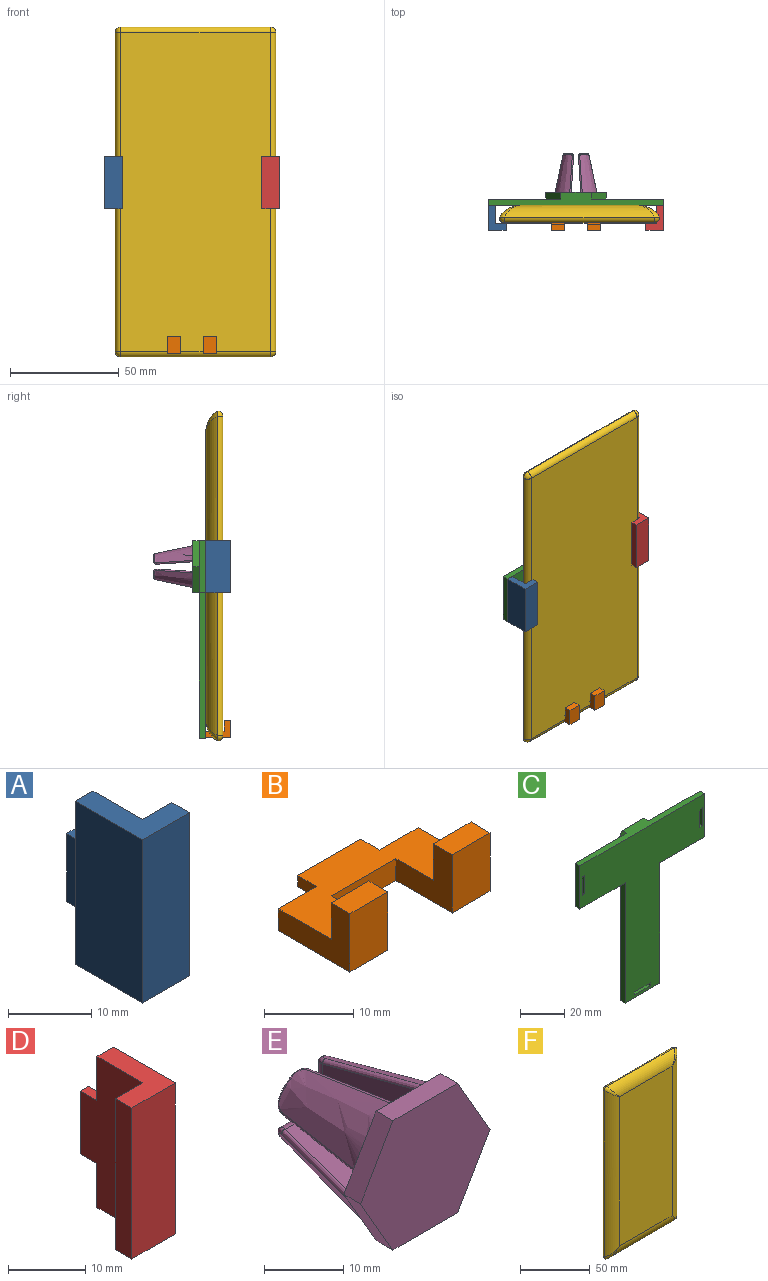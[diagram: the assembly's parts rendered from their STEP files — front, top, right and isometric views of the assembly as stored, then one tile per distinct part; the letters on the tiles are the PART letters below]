
ASSEMBLY  parts=6 mates=5
PART A: 12 faces, bbox 8x14.4x24 mm
  f0: plane 11.4x8mm, normal (0,0,-1), area 49.2mm2, adj f1,f4,f5,f6,f7,f11
  f1: plane 24x11.4mm, normal (1,0,0), area 231.6mm2, adj f0,f2,f3,f7,f8,f10,f11
  f2: plane 11.4x8mm, normal (0,0,1), area 49.2mm2, adj f1,f4,f5,f6,f7,f11
  f3: plane 10x1.5mm, normal (0,1,0), area 15mm2, adj f1,f8,f9,f10
  f4: plane 24x11.4mm, normal (-1,0,0), area 273.6mm2, adj f0,f2,f6,f11
  f5: plane 24x3mm, normal (1,0,0), area 72mm2, adj f0,f2,f6,f7
  f6: plane 24x8mm, normal (0,-1,0), area 192mm2, adj f0,f2,f4,f5
  f7: plane 24x5mm, normal (0,1,0), area 120mm2, adj f0,f1,f2,f5
  f8: plane 3x1.5mm, normal (0,0,1), area 4.5mm2, adj f1,f3,f9,f11
  f9: plane 10x3mm, normal (-1,0,0), area 30mm2, adj f3,f8,f10,f11
  f10: plane 3x1.5mm, normal (0,0,-1), area 4.5mm2, adj f1,f3,f9,f11
  f11: plane 24x3mm, normal (0,1,0), area 57mm2, adj f0,f1,f2,f4,f8,f9,f10
PART B: 18 faces, bbox 22.2x14.4x8 mm
  f0: plane 10x1.5mm, normal (0,1,0), area 15mm2, adj f1,f2,f3,f4
  f1: plane 22.2x11.4mm, normal (0,0,1), area 156.3mm2, adj f0,f3,f4,f5,f6,f7,f9,f12
  f2: plane 10x3mm, normal (0,0,-1), area 30mm2, adj f0,f3,f4,f5
  f3: plane 3x1.5mm, normal (-1,0,0), area 4.5mm2, adj f0,f1,f2,f5
  f4: plane 3x1.5mm, normal (1,0,0), area 4.5mm2, adj f0,f1,f2,f5
  f5: plane 22.2x3mm, normal (0,1,0), area 51.6mm2, adj f1,f2,f3,f4,f7,f8,f16
  f6: plane 8.9x8mm, normal (1,0,0), area 41.7mm2, adj f1,f8,f9,f10,f11,f17
  f7: plane 11.4x8mm, normal (-1,0,0), area 49.2mm2, adj f1,f5,f8,f9,f10,f11
  f8: plane 22.2x11.4mm, normal (0,0,-1), area 162.3mm2, adj f5,f6,f7,f11,f12,f15,f16,f17
  f9: plane 6x5mm, normal (0,1,0), area 30mm2, adj f1,f6,f7,f10
  f10: plane 6x3mm, normal (0,0,1), area 18mm2, adj f6,f7,f9,f11
  f11: plane 8x6mm, normal (0,-1,0), area 48mm2, adj f6,f7,f8,f10
  f12: plane 8.9x8mm, normal (-1,0,0), area 41.7mm2, adj f1,f8,f13,f14,f15,f17
  f13: plane 6x5mm, normal (0,1,0), area 30mm2, adj f1,f12,f14,f16
  f14: plane 6x3mm, normal (0,0,1), area 18mm2, adj f12,f13,f15,f16
  f15: plane 8x6mm, normal (0,-1,0), area 48mm2, adj f8,f12,f14,f16
  f16: plane 11.4x8mm, normal (1,0,0), area 49.2mm2, adj f1,f5,f8,f13,f14,f15
  f17: plane 10.2x3mm, normal (0,-1,0), area 30.6mm2, adj f1,f6,f8,f12
PART C: 35 faces, bbox 80.2x6x90.8 mm
  f0: plane 66.75x3mm, normal (-1,0,0), area 200.2mm2, adj f2,f3,f4,f5
  f1: plane 66.75x3mm, normal (1,0,0), area 200.2mm2, adj f2,f3,f4,f9
  f2: plane 22.2x3mm, normal (0,0,-1), area 66.6mm2, adj f0,f1,f3,f4
  f3: plane 90.75x80.2mm, normal (0,1,0), area 2859.3mm2, adj f0,f1,f2,f5,f6,f7,f8,f9
  f4: plane 90.75x80.2mm, normal (0,-1,0), area 3358.2mm2, adj f0,f1,f2,f5,f6,f7,f8,f9
  f5: plane 29x3mm, normal (0,0,-1), area 87mm2, adj f0,f3,f4,f8
  f6: plane 24x3mm, normal (1,0,0), area 72mm2, adj f3,f4,f7,f9
  f7: plane 80.2x6mm, normal (0,0,1), area 282.2mm2, adj f3,f4,f6,f8,f16,f17,f21
  f8: plane 24x3mm, normal (-1,0,0), area 72mm2, adj f3,f4,f5,f7
  f9: plane 29x3mm, normal (0,0,-1), area 87mm2, adj f1,f3,f4,f6
  f10: plane 10.1x5.83mm, normal (0.87,0,-0.5), area 35mm2, adj f11,f20,f21,f22
  f11: plane 10.1x5.83mm, normal (0.87,0,0.5), area 35mm2, adj f10,f12,f21,f22
  f12: plane 11.66x3mm, normal (0,0,1), area 35mm2, adj f11,f13,f21,f22
  f13: plane 10.1x5.83mm, normal (-0.87,0,0.5), area 35mm2, adj f12,f14,f21,f22
  f14: plane 10.1x5.83mm, normal (-0.87,0,-0.5), area 35mm2, adj f13,f20,f21,f22
  f15: plane 12x6.93mm, normal (-0.87,0,-0.5), area 41.6mm2, adj f3,f16,f19,f21
  f16: plane 12x6.93mm, normal (-0.87,0,0.5), area 41.6mm2, adj f3,f7,f15,f21
  f17: plane 12x6.93mm, normal (0.87,0,0.5), area 41.6mm2, adj f3,f7,f18,f21
  f18: plane 12x6.93mm, normal (0.87,0,-0.5), area 41.6mm2, adj f3,f17,f19,f21
  f19: plane 13.86x3mm, normal (0,0,-1), area 41.6mm2, adj f3,f15,f18,f21
  f20: plane 11.66x3mm, normal (0,0,-1), area 35mm2, adj f10,f14,f21,f22
  f21: plane 27.71x24mm, normal (0,1,0), area 145.5mm2, adj f7,f10,f11,f12,f13,f14,f15,f16
  f22: plane 23.33x20.2mm, normal (0,1,0), area 353.4mm2, adj f10,f11,f12,f13,f14,f20
  f23: plane 10.1x3mm, normal (1,0,0), area 30.3mm2, adj f3,f4,f24,f25
  f24: plane 3x1.6mm, normal (0,0,-1), area 4.8mm2, adj f3,f4,f23,f26
  f25: plane 3x1.6mm, normal (0,0,1), area 4.8mm2, adj f3,f4,f23,f26
  f26: plane 10.1x3mm, normal (-1,0,0), area 30.3mm2, adj f3,f4,f24,f25
  f27: plane 10.1x3mm, normal (0,0,1), area 30.3mm2, adj f3,f4,f28,f29
  f28: plane 3x1.6mm, normal (1,0,0), area 4.8mm2, adj f3,f4,f27,f30
  f29: plane 3x1.6mm, normal (-1,0,0), area 4.8mm2, adj f3,f4,f27,f30
  f30: plane 10.1x3mm, normal (0,0,-1), area 30.3mm2, adj f3,f4,f28,f29
  f31: plane 10.1x3mm, normal (1,0,0), area 30.3mm2, adj f3,f4,f32,f33
  f32: plane 3x1.6mm, normal (0,0,-1), area 4.8mm2, adj f3,f4,f31,f34
  f33: plane 3x1.6mm, normal (0,0,1), area 4.8mm2, adj f3,f4,f31,f34
  f34: plane 10.1x3mm, normal (-1,0,0), area 30.3mm2, adj f3,f4,f32,f33
PART D: 12 faces, bbox 8x14.4x24 mm
  f0: plane 11.4x8mm, normal (0,0,-1), area 49.2mm2, adj f1,f3,f5,f6,f7,f11
  f1: plane 24x11.4mm, normal (1,0,0), area 273.6mm2, adj f0,f4,f6,f11
  f2: plane 10x1.5mm, normal (0,1,0), area 15mm2, adj f3,f8,f9,f10
  f3: plane 24x11.4mm, normal (-1,0,0), area 231.6mm2, adj f0,f2,f4,f7,f8,f10,f11
  f4: plane 11.4x8mm, normal (0,0,1), area 49.2mm2, adj f1,f3,f5,f6,f7,f11
  f5: plane 24x3mm, normal (-1,0,0), area 72mm2, adj f0,f4,f6,f7
  f6: plane 24x8mm, normal (0,-1,0), area 192mm2, adj f0,f1,f4,f5
  f7: plane 24x5mm, normal (0,1,0), area 120mm2, adj f0,f3,f4,f5
  f8: plane 3x1.5mm, normal (0,0,-1), area 4.5mm2, adj f2,f3,f9,f11
  f9: plane 10x3mm, normal (1,0,0), area 30mm2, adj f2,f8,f10,f11
  f10: plane 3x1.5mm, normal (0,0,1), area 4.5mm2, adj f2,f3,f9,f11
  f11: plane 24x3mm, normal (0,1,0), area 57mm2, adj f0,f1,f3,f4,f8,f9,f10
PART E: 60 faces, bbox 23.2x23.4x20.6 mm
  f0: bspline ~17.61x8.12mm, area 143.4mm2, adj f4,f18,f19,f20,f48,f52
  f1: bspline ~17.61x8.12mm, area 143.4mm2, adj f4,f22,f23,f24,f43,f47
  f2: bspline ~17.61x8.12mm, area 143.4mm2, adj f4,f26,f27,f28,f38,f42
  f3: bspline ~17.61x8.12mm, area 143.4mm2, adj f4,f30,f31,f32,f33,f37
  f4: plane 23.15x20.06mm, normal (0,1,0), area 188.5mm2, adj f0,f1,f2,f3,f6,f7,f9,f10
  f5: plane 2.36x2.36mm, normal (0,1,0), area 3.3mm2, adj f31,f34,f36
  f6: plane 16.4x7.48mm, normal (-1,-0.07,0), area 85.4mm2, adj f4,f29,f32,f34
  f7: plane 16.4x7.48mm, normal (0,-0.07,-1), area 85.4mm2, adj f4,f29,f30,f36
  f8: plane 2.36x2.36mm, normal (0,1,0), area 3.3mm2, adj f27,f39,f41
  f9: plane 16.4x7.48mm, normal (1,-0.07,0), area 85.4mm2, adj f4,f25,f28,f39
  f10: plane 16.4x7.48mm, normal (0,-0.07,-1), area 85.4mm2, adj f4,f25,f26,f41
  f11: plane 2.36x2.36mm, normal (0,1,0), area 3.3mm2, adj f23,f44,f46
  f12: plane 16.4x7.48mm, normal (-1,-0.07,0), area 85.4mm2, adj f4,f21,f24,f44
  f13: plane 16.4x7.48mm, normal (0,-0.07,1), area 85.4mm2, adj f4,f21,f22,f46
  f14: plane 2.36x2.36mm, normal (0,1,0), area 3.3mm2, adj f19,f49,f51
  f15: plane 16.4x7.48mm, normal (0,-0.07,1), area 85.4mm2, adj f4,f17,f20,f49
  f16: plane 16.4x7.48mm, normal (1,-0.07,0), area 85.4mm2, adj f4,f17,f18,f51
  f17: cylinder r=0.5mm len=16.41mm, axis (-0.07,-1,-0.07), area 12.9mm2, adj f4,f15,f16,f50
  f18: bspline ~22.72x5.45mm, area 15.7mm2, adj f0,f4,f16,f52
  f19: bspline ~3.89x3.54mm, area 2.4mm2, adj f0,f14,f48,f52
  f20: bspline ~22.72x5.45mm, area 15.7mm2, adj f0,f4,f15,f48
  f21: cylinder r=0.5mm len=16.41mm, axis (0.07,-1,-0.07), area 12.9mm2, adj f4,f12,f13,f45
  f22: bspline ~22.72x5.45mm, area 15.7mm2, adj f1,f4,f13,f47
  f23: bspline ~3.89x3.54mm, area 2.4mm2, adj f1,f11,f43,f47
  f24: bspline ~22.72x5.45mm, area 15.7mm2, adj f1,f4,f12,f43
  f25: cylinder r=0.5mm len=16.41mm, axis (-0.07,-1,0.07), area 12.9mm2, adj f4,f9,f10,f40
  f26: bspline ~22.72x5.45mm, area 15.7mm2, adj f2,f4,f10,f42
  f27: bspline ~3.89x3.54mm, area 2.4mm2, adj f2,f8,f38,f42
  f28: bspline ~22.72x5.45mm, area 15.7mm2, adj f2,f4,f9,f38
  f29: cylinder r=0.5mm len=16.41mm, axis (-0.07,1,-0.07), area 12.9mm2, adj f4,f6,f7,f35
  f30: bspline ~20.18x4.91mm, area 15.7mm2, adj f3,f4,f7,f37
  f31: bspline ~3.62x3.43mm, area 2.4mm2, adj f3,f5,f33,f37
  f32: bspline ~20.18x4.91mm, area 15.7mm2, adj f3,f4,f6,f33
  f33: bspline ~2.03x1.75mm, area 1.9mm2, adj f3,f31,f32,f34
  f34: cylinder r=1.5mm len=4mm, axis (0,0,-1), area 7.8mm2, adj f5,f6,f33,f35
  f35: bspline ~1.76x1.5mm, area 0.9mm2, adj f29,f34,f36
  f36: cylinder r=1.5mm len=4mm, axis (-1,0,0), area 7.8mm2, adj f5,f7,f35,f37
  f37: bspline ~1.99x1.93mm, area 1.9mm2, adj f3,f30,f31,f36
  f38: bspline ~1.99x1.93mm, area 1.9mm2, adj f2,f27,f28,f39
  f39: cylinder r=1.5mm len=4mm, axis (0,0,-1), area 7.8mm2, adj f8,f9,f38,f40
  f40: bspline ~1.76x1.5mm, area 0.9mm2, adj f25,f39,f41
  f41: cylinder r=1.5mm len=4mm, axis (1,0,0), area 7.8mm2, adj f8,f10,f40,f42
  f42: bspline ~2.03x1.75mm, area 1.9mm2, adj f2,f26,f27,f41
  f43: bspline ~1.99x1.93mm, area 1.9mm2, adj f1,f23,f24,f44
  f44: cylinder r=1.5mm len=4mm, axis (0,0,1), area 7.8mm2, adj f11,f12,f43,f45
  f45: bspline ~1.76x1.5mm, area 0.9mm2, adj f21,f44,f46
  f46: cylinder r=1.5mm len=4mm, axis (-1,0,0), area 7.8mm2, adj f11,f13,f45,f47
  f47: bspline ~2.03x1.75mm, area 1.9mm2, adj f1,f22,f23,f46
  f48: bspline ~1.99x1.93mm, area 1.9mm2, adj f0,f19,f20,f49
  f49: cylinder r=1.5mm len=4mm, axis (1,0,0), area 7.8mm2, adj f14,f15,f48,f50
  f50: bspline ~1.76x1.5mm, area 0.9mm2, adj f17,f49,f51
  f51: cylinder r=1.5mm len=4mm, axis (0,0,1), area 7.8mm2, adj f14,f16,f50,f52
  f52: bspline ~2.03x1.75mm, area 1.9mm2, adj f0,f18,f19,f51
  f53: plane 11.55x3mm, normal (0,0,1), area 34.6mm2, adj f4,f54,f58,f59
  f54: plane 10x5.77mm, normal (0.87,0,0.5), area 34.6mm2, adj f4,f53,f55,f59
  f55: plane 10x5.77mm, normal (0.87,0,-0.5), area 34.6mm2, adj f4,f54,f56,f59
  f56: plane 11.55x3mm, normal (0,0,-1), area 34.6mm2, adj f4,f55,f57,f59
  f57: plane 10x5.77mm, normal (-0.87,0,-0.5), area 34.6mm2, adj f4,f56,f58,f59
  f58: plane 10x5.77mm, normal (-0.87,0,0.5), area 34.6mm2, adj f4,f53,f57,f59
  f59: plane 23.09x20mm, normal (0,-1,0), area 346.4mm2, adj f53,f54,f55,f56,f57,f58
PART F: 18 faces, bbox 73.7x7.9x151.5 mm
  f0: plane 131.46x53.66mm, normal (0,-1,0), area 7053.4mm2, adj f10,f13,f14,f17
  f1: plane 146.5x68.7mm, normal (0,1,0), area 10064.6mm2, adj f3,f4,f7,f8
  f2: sphere r=2.5mm, area 9.8mm2, adj f3,f4,f11
  f3: cylinder r=2.5mm len=68.7mm, axis (-1,0,0), area 269.8mm2, adj f1,f2,f5,f13
  f4: cylinder r=2.5mm len=146.5mm, axis (0,0,-1), area 575.3mm2, adj f1,f2,f6,f10
  f5: sphere r=2.5mm, area 13.4mm2, adj f3,f7,f15
  f6: sphere r=2.5mm, area 9.8mm2, adj f4,f8,f12
  f7: cylinder r=2.5mm len=146.5mm, axis (0,0,1), area 575.3mm2, adj f1,f5,f9,f17
  f8: cylinder r=2.5mm len=68.7mm, axis (1,0,0), area 269.8mm2, adj f1,f6,f9,f14
  f9: sphere r=2.5mm, area 6.2mm2, adj f7,f8,f16
  f10: cylinder r=12mm len=146.5mm, axis (0,0,-1), area 1648.4mm2, adj f0,f4,f11,f12
  f11: bspline ~10.02x10.02mm, area 18.9mm2, adj f2,f10,f13
  f12: bspline ~10.02x10.02mm, area 18.8mm2, adj f6,f10,f14
  f13: cylinder r=12mm len=68.7mm, axis (1,0,0), area 725.6mm2, adj f0,f3,f11,f15
  f14: cylinder r=12mm len=68.7mm, axis (1,0,0), area 725.6mm2, adj f0,f8,f12,f16
  f15: bspline ~10.02x10.02mm, area 18.9mm2, adj f5,f13,f17
  f16: bspline ~10.02x10.02mm, area 18.9mm2, adj f9,f14,f17
  f17: cylinder r=12mm len=146.5mm, axis (0,0,-1), area 1648.4mm2, adj f0,f7,f15,f16
PLACE A t=(-81.2,-40.39,27.55)mm
PLACE B t=(-94.2,-40.39,40.65)mm
PLACE C t=(-94.2,-40.39,27.55)mm
PLACE D t=(-107.2,-40.39,27.55)mm
PLACE E t=(-94.2,-57.39,27.55)mm
PLACE F rot(axis=(1,0,0),180deg) t=(-232.27,-68.29,-8.84)mm
MATE fastened B.f0 <-> C.f3  axis (0,1,0) through (-94.2,-57.39,-48.1)mm
MATE fastened E.f59 <-> C.f22  axis (0,-1,0) through (-94.2,-57.39,27.55)mm
MATE planar C.f4 <-> F.f0  axis (0,-1,0) through (-94.2,-60.39,7.9)mm
MATE fastened D.f2 <-> C.f3  axis (0,1,0) through (-55.6,-57.39,27.55)mm
MATE fastened A.f3 <-> C.f3  axis (0,1,0) through (-132.8,-57.39,27.55)mm
